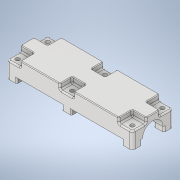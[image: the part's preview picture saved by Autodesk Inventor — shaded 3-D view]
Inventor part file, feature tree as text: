
AUTODESK INVENTOR PART (.ipt)
format: ipt  version: 2020.2 (Build 242310000, 310)  size: 783,872 bytes
history: native  units: mm
features: sketch x14, extrude x13, projected_geometry x9, fillet x3, other x1, mirror x1, boolean_combine x1
ambient origin geometry x8: Origin, YZ Plane, XZ Plane, XY Plane, X Axis, Y Axis, Z Axis, Center Point
bodies: Volumenkörper1 (feature_tree), Solid2 (feature_tree), Solid3 (feature_tree)
feature tree (42):
  extrude  "Extrusion1"  Depth=6.0mm
  other  "Spirale1"
  mirror  "Spiegeln1"
  extrude  "Extrusion5"  Depth=10.0mm
  extrude  "Extrusion6"  Depth=1.0mm
  boolean_combine  "Combine1"
  extrude  "Extrusion7"  Depth=10.0mm TaperAngle=0.0deg
  extrude  "Extrusion8"  Depth=100.0mm TaperAngle=0.0deg
  extrude  "Extrusion9"  Depth=24.0mm
  extrude  "Extrusion10"  Depth=12.0mm TaperAngle=0.0deg
  extrude  "Extrusion11"  Depth=4.0mm
  extrude  "Extrusion13"  Depth=10.0mm
  fillet  "Fillet2"  Radius=10.0mm
  fillet  "Fillet3"  Radius=77.15mm
  fillet  "Fillet4"  Radius=30.0mm
  extrude  "Extrusion14"  Depth=6.0mm
  extrude  "Extrusion15"  Depth=10.0mm TaperAngle=0.0deg
  extrude  "Extrusion16"  Depth=3.0mm
  extrude  "Extrusion17"  Depth=1.0mm
  sketch  "Skizze1"  dims[d0=6.0mm d1=11.0mm]
  sketch  "Skizze3"  dims[d2=36.0mm d3=0.0mm]
  projected_geometry  "Projizierte Kontur2"
  sketch  "Sketch7"  dims[d8=7.0mm d9=24.5mm d10=10.0mm d11=0.0mm d12=90.0deg d13=90.0deg d14=0.0mm d15=0.0mm d16=4.0mm]
  sketch  "Sketch8"  dims[d17=13.962634mm d18=1.0mm]
  sketch  "Sketch9"  dims[d19=0.1mm d32=10.0mm d33=0.0mm]
  projected_geometry  "Projected Loop4"
  sketch  "Sketch10"  dims[d34=7.0mm d35=100.0mm d36=0.0mm]
  sketch  "Sketch11"  dims[d37=82.0mm d38=0.0mm d39=24.0mm]
  projected_geometry  "Projected Loop5"
  projected_geometry  "Projected Loop6"
  sketch  "Sketch12"  dims[d40=30.0mm d41=12.0mm d42=0.0mm]
  sketch  "Sketch13"  dims[d43=3.0mm d44=4.0mm]
  projected_geometry  "Projected Loop7"
  projected_geometry  "Projected Loop8"
  sketch  "Sketch15"  dims[d45=4.0mm d46=20.0mm d48=22.0mm d49=20.0mm d51=84.0mm d54=10.0mm d55=0.0mm d56=77.15mm d57=30.0mm]
  sketch  "Sketch16"  dims[d62=4.0mm d63=0.0mm d64=6.0mm]
  projected_geometry  "Projected Loop10"
  sketch  "Sketch17"  dims[d65=10.0mm d66=0.0mm d67=10.0mm d68=0.0mm]
  projected_geometry  "Projected Loop11"
  projected_geometry  "Projected Loop12"
  sketch  "Sketch18"  dims[d76=3.0mm d77=3.0mm]
  sketch  "Sketch19"  dims[d78=4.0mm d79=48.0mm d80=46.0mm d81=4.0mm d85=7.0mm d86=6.9mm d87=3.5mm d88=7.0mm d89=6.9mm d90=3.5mm d91=10.0mm d92=10.0mm d93=10.0mm d94=10.0mm d95=10.0mm d96=10.0mm d97=10.0mm d98=10.0mm d99=10.0mm d100=10.0mm d101=10.0mm d102=10.0mm d103=4.0mm d104=0.0mm d105=1.0mm d106=1.0mm d107=2.0mm d108=0.5mm d109=6.5mm d110=2.1mm d111=0.0mm d112=6.5mm d113=2.1mm d114=0.0mm d115=180.0deg d116=6.9mm d117=6.9mm d118=6.9mm d119=6.9mm d120=12.0mm d121=0.2mm d122=0.0mm d123=15.0mm d124=0.2mm d125=0.0mm d126=7.9mm d127=0.0mm d128=7.9mm d129=0.0mm]
